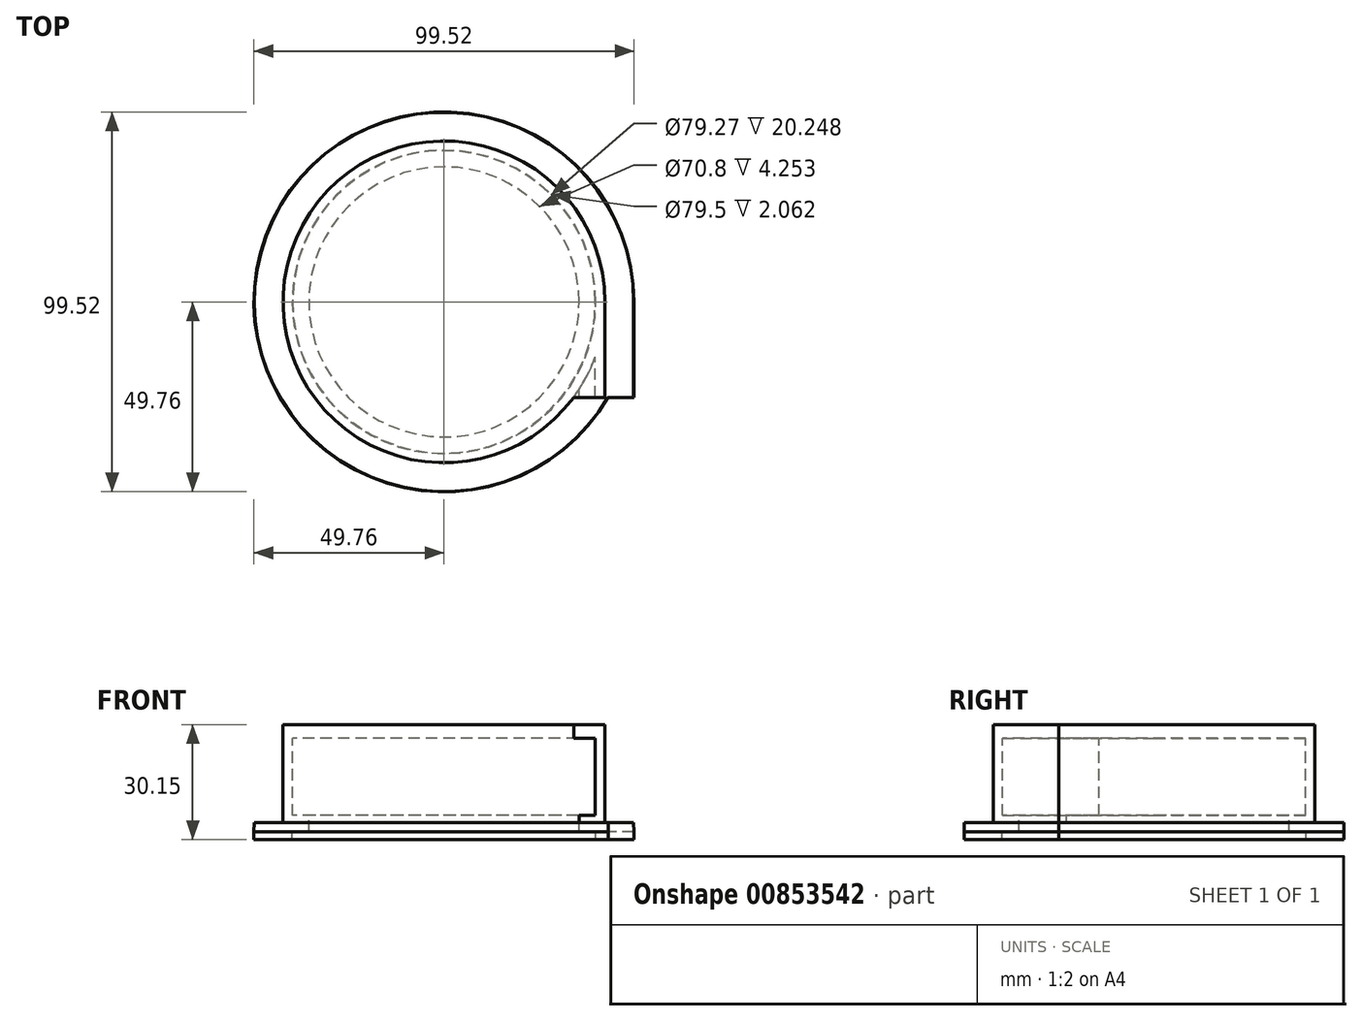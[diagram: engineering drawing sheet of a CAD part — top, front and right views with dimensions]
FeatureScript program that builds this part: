
annotation { "Feature Type Name" : "Feature", "Feature Type Description" : "" }
export const myFeature = defineFeature(function(context is Context, id is Id, definition is map)
    precondition{}
    {
        {
            var Q0;
            Q0=qCreatedBy(makeId("Front.planeOp"),FACE);
            var sketch = newSketch(context, id + "F0", { "sketchPlane" : qUnion([Q0])});
            skLineSegment(sketch, "E0", {"start": v(0, 36.46) * mm, "end": v(42.16, 36.46) * mm});
            skLineSegment(sketch, "E1", {"start": v(42.16, 36.46) * mm, "end": v(42.16, 12.63) * mm});
            skLineSegment(sketch, "E2", {"start": v(39.63, 12.63) * mm, "end": v(35.4, 12.63) * mm});
            skLineSegment(sketch, "E3", {"start": v(35.4, 12.63) * mm, "end": v(35.4, 8.38) * mm});
            skLineSegment(sketch, "E4", {"start": v(35.4, 8.38) * mm, "end": v(39.75, 8.38) * mm});
            skLineSegment(sketch, "E5", {"start": v(42.16, 10.77) * mm, "end": v(42.16, 14.72) * mm});
            skLineSegment(sketch, "E6", {"start": v(42.16, 14.72) * mm, "end": v(42.16, 10.77) * mm});
            skLineSegment(sketch, "E7", {"start": v(39.75, 6.43) * mm, "end": v(39.75, 6.31) * mm});
            skLineSegment(sketch, "E8", {"start": v(39.75, 6.31) * mm, "end": v(49.76, 6.31) * mm});
            skLineSegment(sketch, "E9", {"start": v(49.76, 6.31) * mm, "end": v(49.76, 8.38) * mm});
            skLineSegment(sketch, "E10", {"start": v(39.63, 12.63) * mm, "end": v(39.63, 32.88) * mm});
            skLineSegment(sketch, "E11", {"start": v(39.63, 32.88) * mm, "end": v(0, 32.88) * mm});
            skLineSegment(sketch, "E12", {"start": v(0, 32.88) * mm, "end": v(0, 36.46) * mm});
            skLineSegment(sketch, "E13", {"start": v(42.16, 10.77) * mm, "end": v(49.68, 10.77) * mm});
            skLineSegment(sketch, "E14", {"start": v(49.76, 8.38) * mm, "end": v(49.68, 10.77) * mm});
            skLineSegment(sketch, "E15", {"start": v(39.75, 6.43) * mm, "end": v(39.75, 8.38) * mm});
            skPoint(sketch, "E16.orphan", {"position": v(42.16, 8.38) * mm});
            skLineSegment(sketch, "E17", {"start": v(0, 40.44) * mm, "end": v(0, 0) * mm, "construction": true});
            skSolve(sketch);
        }
        {
            var Q0;
            Q0 = qSketchRegion(id + "F0", true);
            extrude(context, id + "F1", {"entities" : qUnion([Q0]), "depth" : 25 * mm, "offsetDistance" : 25 * mm});
        }
        {
            var Q0;
            Q0 = qSketchRegion(id + "F0", true);
            var Q1;
            Q1=sQuery(id+"F0.wireOp",EDGE,"E17");
            revolve(context, id + "F2", {"operationType" : NewBodyOperationType.ADD, "surfaceOperationType" : NewSurfaceOperationType.NEW, "entities" : qUnion([Q0]), "axis" : qUnion([Q1]), "revolveType" : RevolveType.FULL});
        }
    });
